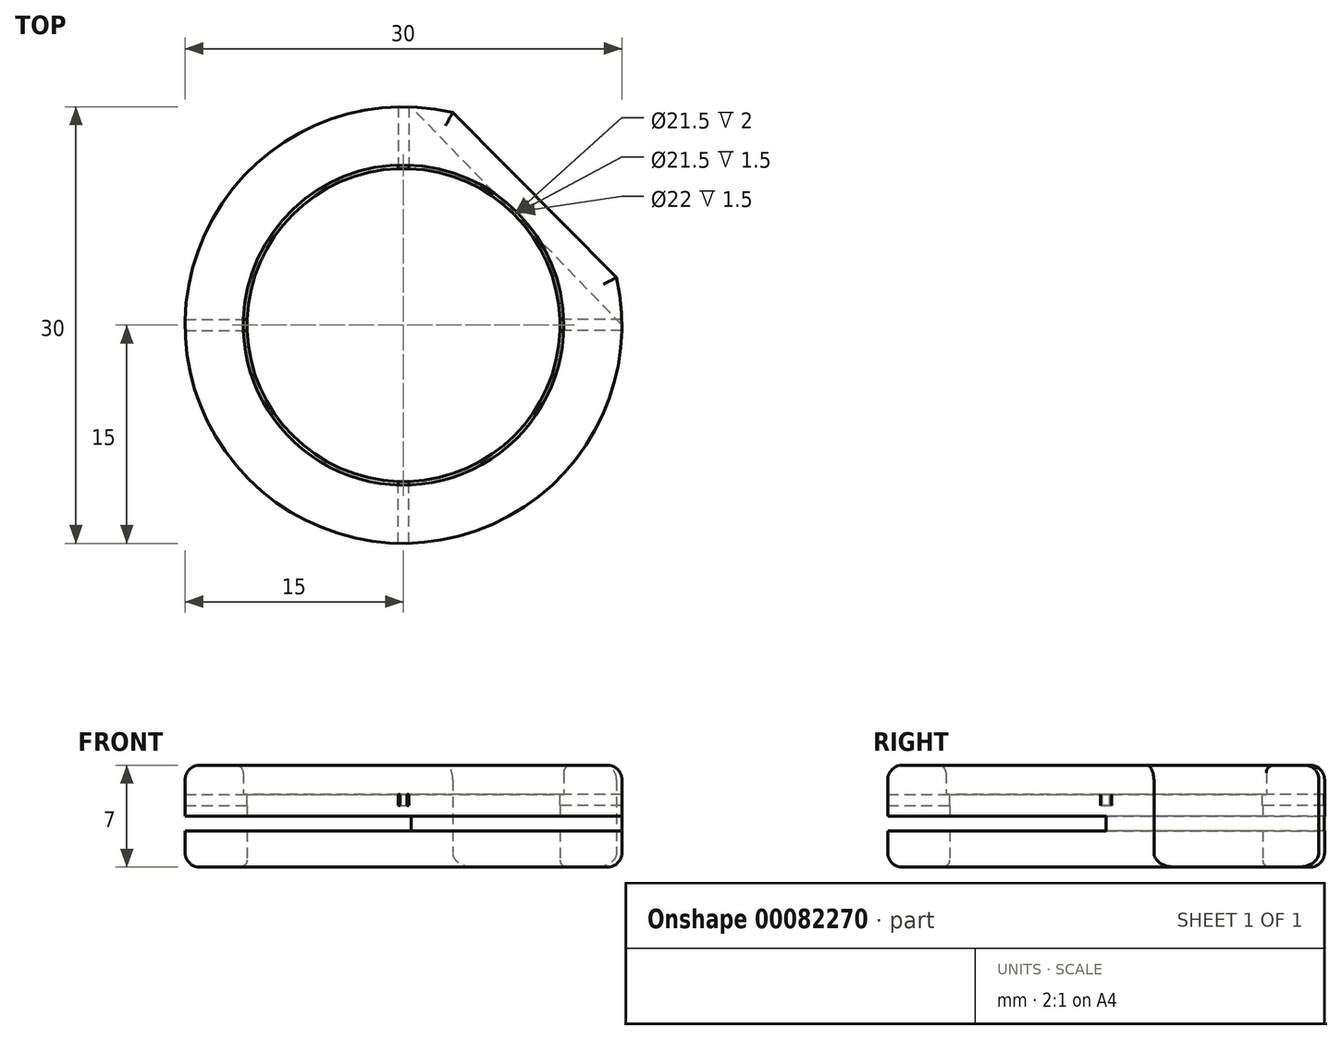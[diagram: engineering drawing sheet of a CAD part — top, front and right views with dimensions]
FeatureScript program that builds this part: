
annotation { "Feature Type Name" : "Feature", "Feature Type Description" : "" }
export const myFeature = defineFeature(function(context is Context, id is Id, definition is map)
    precondition{}
    {
        {
            var Q0;
            Q0=qCreatedBy(makeId("Top.planeOp"),FACE);
            var sketch = newSketch(context, id + "F0", { "sketchPlane" : qUnion([Q0])});
            skCircle(sketch, "E0", {"center": v(0, 0) * mm, "radius": 10.75 * mm});
            skCircle(sketch, "E1", {"center": v(0, 0) * mm, "radius": 15 * mm});
            skSolve(sketch);
        }
        {
            var Q0;
            Q0=makeQuery(id+"F0.imprint","IMPRINT",FACE,{"disambiguationData":[TD([[makeQuery(id+"F0.imprint","IMPRINT",EDGE,{"derivedFrom":sQuery(id+"F0.wireOp",EDGE,"E0")}),-1.0]])]});
            extrude(context, id + "F1", {"entities" : qUnion([Q0]), "depth" : 5 * mm});
        }
        {
            var Q0;
            Q0=makeQuery(id+"F1.opExtrude","CAP_FACE",FACE,{"disambiguationData":[OSD([sQuery(id+"F0.wireOp",EDGE,"E0"),sQuery(id+"F0.wireOp",EDGE,"E1")])],"isStart":false});
            var sketch = newSketch(context, id + "F2", { "sketchPlane" : qUnion([Q0])});
            skLineSegment(sketch, "E2.bottom", {"start": v(0.37, 15) * mm, "end": v(-0.38, 15) * mm});
            skLineSegment(sketch, "E2.top", {"start": v(0.37, 10) * mm, "end": v(-0.38, 10) * mm});
            skLineSegment(sketch, "E2.left", {"start": v(0.37, 15) * mm, "end": v(0.37, 10) * mm});
            skLineSegment(sketch, "E2.right", {"start": v(-0.38, 15) * mm, "end": v(-0.38, 10) * mm});
            skPoint(sketch, "E2.middle", {"position": v(0, 12.5) * mm});
            skLineSegment(sketch, "E3", {"start": v(15, 15) * mm, "end": v(0.27, 0) * mm, "construction": true});
            skLineSegment(sketch, "E4", {"start": v(3.4, 14.61) * mm, "end": v(14.64, 3.28) * mm});
            skLineSegment(sketch, "E5", {"start": v(3.36, 14.58) * mm, "end": v(5.02, 16.23) * mm});
            skLineSegment(sketch, "E6", {"start": v(5.02, 16.23) * mm, "end": v(16.27, 4.9) * mm});
            skLineSegment(sketch, "E7", {"start": v(14.6, 3.25) * mm, "end": v(16.27, 4.9) * mm});
            skLineSegment(sketch, "E8.1.0", {"start": v(-14.5, -0.38) * mm, "end": v(-14.5, 0.37) * mm});
            skPoint(sketch, "E8.1.1", {"position": v(-12.5, 0) * mm});
            skLineSegment(sketch, "E8.1.2", {"start": v(-15, 0.37) * mm, "end": v(-10, 0.37) * mm});
            skLineSegment(sketch, "E8.1.3", {"start": v(-15, -0.38) * mm, "end": v(-10, -0.38) * mm});
            skLineSegment(sketch, "E8.1.4", {"start": v(-10, 0.37) * mm, "end": v(-10, -0.38) * mm});
            skLineSegment(sketch, "E8.1.5", {"start": v(-15, 0.37) * mm, "end": v(-15, -0.38) * mm});
            skPoint(sketch, "E8.2.1", {"position": v(0, -12.5) * mm});
            skLineSegment(sketch, "E8.2.2", {"start": v(-0.38, -15) * mm, "end": v(-0.38, -10) * mm});
            skLineSegment(sketch, "E8.2.3", {"start": v(0.37, -15) * mm, "end": v(0.37, -10) * mm});
            skLineSegment(sketch, "E8.2.4", {"start": v(-0.38, -10) * mm, "end": v(0.37, -10) * mm});
            skLineSegment(sketch, "E8.2.5", {"start": v(-0.38, -15) * mm, "end": v(0.37, -15) * mm});
            skPoint(sketch, "E8.3.1", {"position": v(12.5, 0) * mm});
            skLineSegment(sketch, "E8.3.2", {"start": v(15, -0.38) * mm, "end": v(10, -0.38) * mm});
            skLineSegment(sketch, "E8.3.3", {"start": v(15, 0.37) * mm, "end": v(10, 0.37) * mm});
            skLineSegment(sketch, "E8.3.4", {"start": v(10, -0.38) * mm, "end": v(10, 0.37) * mm});
            skLineSegment(sketch, "E8.3.5", {"start": v(15, -0.38) * mm, "end": v(15, 0.37) * mm});
            skPoint(sketch, "E8.center", {"position": v(0, 0) * mm});
            skSolve(sketch);
        }
        {
            var Q0;
            Q0=qCreatedBy(makeId("Top.planeOp"),FACE);
            cPlane(context, id + "F3", {"entities" : qUnion([Q0]), "cplaneType" : CPlaneType.OFFSET, "offset" : 5 * mm, "width" : 150 * mm, "height" : 150 * mm});
        }
        {
            var Q0;
            Q0=qCreatedBy(id+"F3.planeOp",FACE);
            var sketch = newSketch(context, id + "F4", { "sketchPlane" : qUnion([Q0])});
            skPoint(sketch, "E9.0", {"position": v(0, 0) * mm});
            skCircle(sketch, "E10.0", {"center": v(0, 0) * mm, "radius": 10.75 * mm});
            skCircle(sketch, "E11.0", {"center": v(0, 0) * mm, "radius": 15 * mm});
            skCircle(sketch, "E12", {"center": v(0, 0) * mm, "radius": 11 * mm});
            skSolve(sketch);
        }
        {
            var Q0;
            Q0=makeQuery(id+"F4.imprint","IMPRINT",FACE,{"disambiguationData":[TD([[makeQuery(id+"F4.imprint","IMPRINT",EDGE,{"derivedFrom":sQuery(id+"F4.wireOp",EDGE,"E11.0")}),1.0]])]});
            extrude(context, id + "F5", {"entities" : qUnion([Q0]), "operationType" : NewBodyOperationType.ADD, "depth" : 2 * mm});
        }
        {
            var Q0;
            {var subQ0=sQuery(id+"F2.wireOp",EDGE,"E4");Q0=makeQuery(id+"F2.imprint","IMPRINT",FACE,{"disambiguationData":[TD([[makeQuery(id+"F2.imprint","IMPRINT",EDGE,{"derivedFrom":subQ0}),1.0]])]});}
            extrude(context, id + "F6", {"entities" : qUnion([Q0]), "operationType" : NewBodyOperationType.REMOVE, "endBound" : BoundingType.SYMMETRIC, "depth" : 10 * mm});
        }
        {
            var Q0;
            Q0=makeQuery(id+"F6.boolean.opBoolean","INTERSECT",EDGE,{"derivedFrom":[makeQuery(id+"F5.opExtrude","CAP_FACE",FACE,{"disambiguationData":[OSD([sQuery(id+"F4.wireOp",EDGE,"E11.0"),sQuery(id+"F4.wireOp",EDGE,"E12")])],"isStart":false}),makeQuery(id+"F6.opExtrude","SWEPT_FACE",FACE,{"disambiguationData":[OSD([sQuery(id+"F2.wireOp",EDGE,"E4")])]})]});
            var Q1;
            Q1=makeQuery(id+"F6.boolean.opBoolean","COPY",EDGE,{"derivedFrom":makeQuery(id+"F6.opExtrude","CAP_EDGE",EDGE,{"disambiguationData":[OSD([sQuery(id+"F2.wireOp",EDGE,"E4")])],"isStart":true})});
            var Q2;
            Q2=makeQuery(id+"F1.opExtrude","CAP_EDGE",EDGE,{"disambiguationData":[OSD([sQuery(id+"F0.wireOp",EDGE,"E1")])],"isStart":true});
            var Q3;
            Q3=makeQuery(id+"F5.opExtrude","CAP_EDGE",EDGE,{"disambiguationData":[OSD([sQuery(id+"F4.wireOp",EDGE,"E11.0")])],"isStart":false});
            fillet(context, id + "F7", {"entities" : qUnion([Q0, Q1, Q2, Q3]), "radius" : 1 * mm, "tangentPropagation" : true, "allowEdgeOverflow" : false});
        }
        {
            var Q0;
            Q0=makeQuery(id+"F5.opExtrude","CAP_EDGE",EDGE,{"disambiguationData":[OSD([sQuery(id+"F4.wireOp",EDGE,"E12")])],"isStart":false});
            var Q1;
            Q1=makeQuery(id+"F1.opExtrude","CAP_EDGE",EDGE,{"disambiguationData":[OSD([sQuery(id+"F0.wireOp",EDGE,"E0")])],"isStart":true});
            var Q2;
            Q2=makeQuery(id+"F5.opExtrude","CAP_EDGE",EDGE,{"disambiguationData":[OSD([sQuery(id+"F4.wireOp",EDGE,"E10.0")])],"isStart":false});
            fillet(context, id + "F8", {"entities" : qUnion([Q0, Q1, Q2]), "radius" : .5 * mm, "tangentPropagation" : true, "allowEdgeOverflow" : false});
        }
        {
            var Q0;
            {var subQ0=sQuery(id+"F2.wireOp",EDGE,"E8.1.0");Q0=makeQuery(id+"F2.imprint","IMPRINT",FACE,{"disambiguationData":[TD([[makeQuery(id+"F2.imprint","IMPRINT",EDGE,{"derivedFrom":subQ0}),-1.0]])]});}
            var Q1;
            {var subQ4=sQuery(id+"F2.wireOp",EDGE,"E8.1.0");Q1=makeQuery(id+"F2.imprint","IMPRINT",FACE,{"disambiguationData":[TD([[makeQuery(id+"F2.imprint","IMPRINT",EDGE,{"derivedFrom":subQ4}),1.0]])]});}
            var Q2;
            {var subQ0=sQuery(id+"F2.wireOp",EDGE,"E8.2.2");var subQ6=makeQuery(id+"F1.opExtrude","CAP_EDGE",EDGE,{"disambiguationData":[OSD([sQuery(id+"F0.wireOp",EDGE,"E1")])],"isStart":false});var subQ10=makeQuery(id+"F2.imprint","INTERSECT",VERTEX,{"derivedFrom":[subQ6,subQ0]});Q2=makeQuery(id+"F2.imprint","IMPRINT",FACE,{"disambiguationData":[TD([[makeQuery(id+"F2.imprint","IMPRINT",EDGE,{"disambiguationData":[TD([[subQ10,-1.0]])],"derivedFrom":subQ0}),-1.0]])]});}
            var Q3;
            {var subQ1=sQuery(id+"F2.wireOp",EDGE,"E8.3.2");var subQ7=makeQuery(id+"F1.opExtrude","CAP_EDGE",EDGE,{"disambiguationData":[OSD([sQuery(id+"F0.wireOp",EDGE,"E0")])],"isStart":false});var subQ9=makeQuery(id+"F2.imprint","INTERSECT",VERTEX,{"derivedFrom":[subQ7,subQ1]});Q3=makeQuery(id+"F2.imprint","IMPRINT",FACE,{"disambiguationData":[TD([[makeQuery(id+"F2.imprint","IMPRINT",EDGE,{"disambiguationData":[TD([[subQ9,-1.0]])],"derivedFrom":subQ7}),-1.0]])]});}
            var Q4;
            {var subQ0=sQuery(id+"F2.wireOp",EDGE,"E2.bottom");Q4=makeQuery(id+"F2.imprint","IMPRINT",FACE,{"disambiguationData":[TD([[makeQuery(id+"F2.imprint","IMPRINT",EDGE,{"derivedFrom":subQ0}),1.0]])]});}
            extrude(context, id + "F9", {"entities" : qUnion([Q0, Q1, Q2, Q3, Q4]), "operationType" : NewBodyOperationType.REMOVE, "oppositeDirection" : true, "depth" : .75 * mm});
        }
        {
            var Q0;
            Q0=qCreatedBy(id+"F3.planeOp",FACE);
            cPlane(context, id + "F10", {"entities" : qUnion([Q0]), "cplaneType" : CPlaneType.OFFSET, "offset" : 2.5 * mm, "oppositeDirection" : true, "width" : 150 * mm, "height" : 150 * mm});
        }
        {
            var Q0;
            Q0=qCreatedBy(id+"F10.planeOp",FACE);
            var sketch = newSketch(context, id + "F11", { "sketchPlane" : qUnion([Q0])});
            skPoint(sketch, "E13.0", {"position": v(7.63, 7.5) * mm});
            skLineSegment(sketch, "E14", {"start": v(0, 0) * mm, "end": v(7.63, 7.5) * mm, "construction": true});
            skLineSegment(sketch, "E15.bottom", {"start": v(-2.96, -24.58) * mm, "end": v(-24.5, -2.3) * mm});
            skLineSegment(sketch, "E15.top", {"start": v(18.6, -3.72) * mm, "end": v(-2.94, 18.56) * mm});
            skLineSegment(sketch, "E15.left", {"start": v(-2.96, -24.58) * mm, "end": v(18.6, -3.72) * mm});
            skLineSegment(sketch, "E15.right", {"start": v(-24.5, -2.3) * mm, "end": v(-2.94, 18.56) * mm});
            skPoint(sketch, "E15.middle", {"position": v(0, 0) * mm});
            skSolve(sketch);
        }
        {
            var Q0;
            Q0=makeQuery(id+"F11.imprint","IMPRINT",FACE,{"disambiguationData":[TD([[makeQuery(id+"F11.imprint","IMPRINT",EDGE,{"derivedFrom":sQuery(id+"F11.wireOp",EDGE,"E15.bottom")}),-1.0]])]});
            extrude(context, id + "F12", {"entities" : qUnion([Q0]), "operationType" : NewBodyOperationType.REMOVE, "depth" : 1 * mm});
        }
    });
